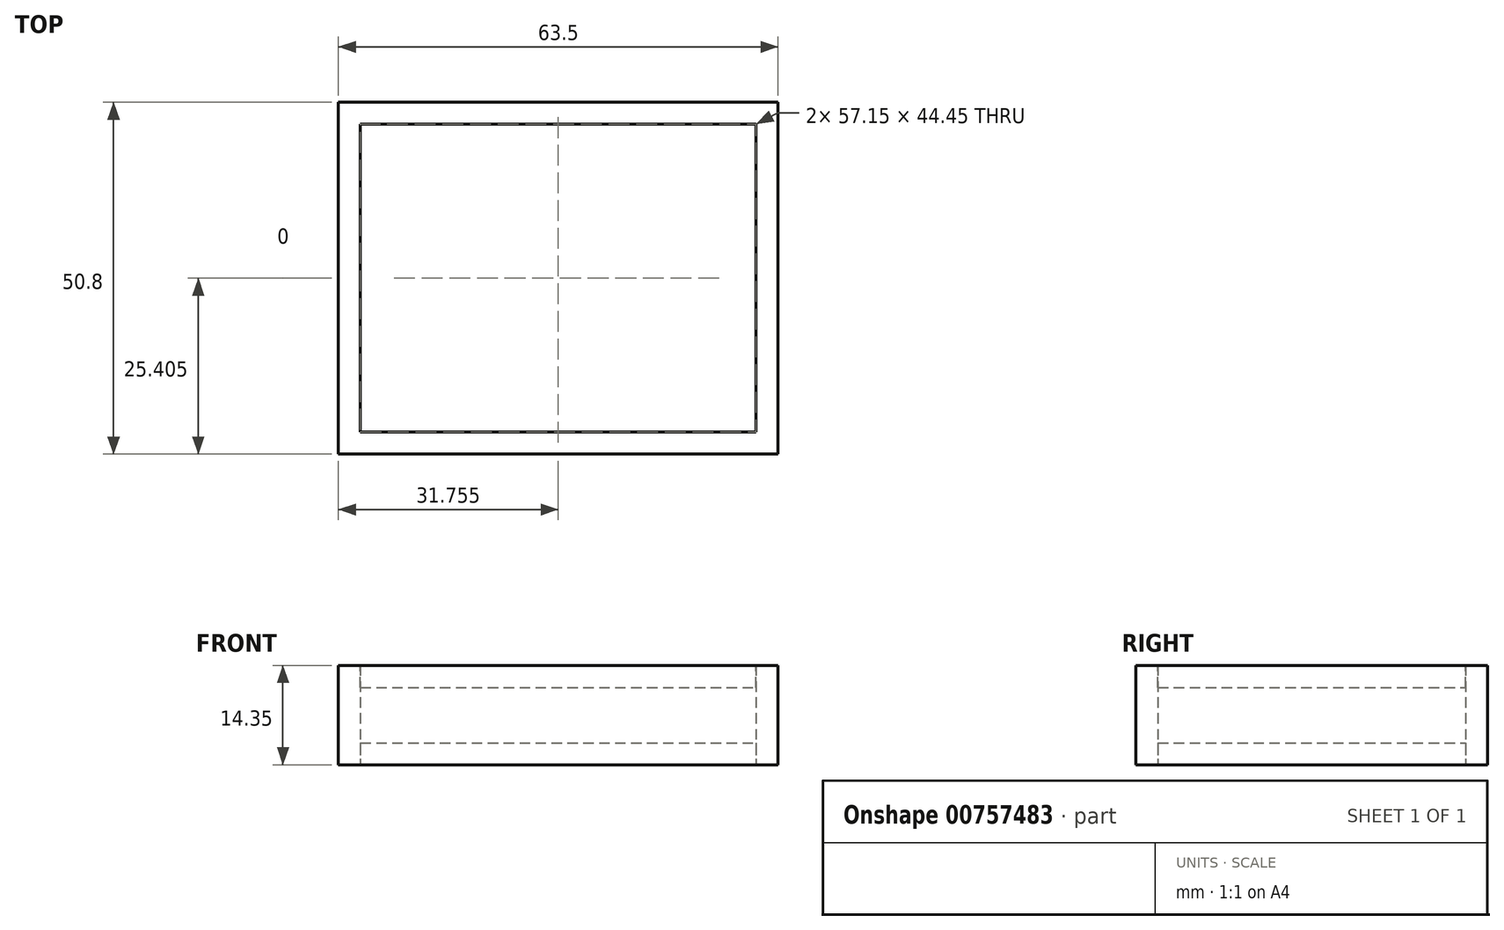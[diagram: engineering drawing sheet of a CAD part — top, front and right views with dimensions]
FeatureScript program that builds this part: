
annotation { "Feature Type Name" : "Feature", "Feature Type Description" : "" }
export const myFeature = defineFeature(function(context is Context, id is Id, definition is map)
    precondition{}
    {
        {
            var Q0;
            Q0=qCreatedBy(makeId("Top.planeOp"),FACE);
            var sketch = newSketch(context, id + "F0", { "sketchPlane" : qUnion([Q0])});
            skLineSegment(sketch, "E0.bottom", {"start": v(0, 0) * mm, "end": v(57.15, 0) * mm});
            skLineSegment(sketch, "E0.top", {"start": v(0, 44.45) * mm, "end": v(57.15, 44.45) * mm});
            skLineSegment(sketch, "E0.left", {"start": v(0, 0) * mm, "end": v(0, 44.45) * mm});
            skLineSegment(sketch, "E0.right", {"start": v(57.15, 0) * mm, "end": v(57.15, 44.45) * mm});
            skLineSegment(sketch, "E1.0", {"start": v(-3.18, 47.63) * mm, "end": v(60.32, 47.63) * mm});
            skLineSegment(sketch, "E1.1", {"start": v(-3.17, -3.17) * mm, "end": v(-3.18, 47.63) * mm});
            skLineSegment(sketch, "E1.2", {"start": v(-3.18, -3.17) * mm, "end": v(60.33, -3.17) * mm});
            skLineSegment(sketch, "E1.3", {"start": v(60.33, -3.17) * mm, "end": v(60.32, 47.62) * mm});
            skSolve(sketch);
        }
        {
            var Q0;
            Q0=makeQuery(id+"F0.imprint","IMPRINT",FACE,{"disambiguationData":[TD([[makeQuery(id+"F0.imprint","IMPRINT",EDGE,{"derivedFrom":sQuery(id+"F0.wireOp",EDGE,"E0.bottom")}),-1.0]])]});
            extrude(context, id + "F1", {"entities" : qUnion([Q0]), "depth" : 8 * mm + 6.35 * mm, "offsetDistance" : 25.4 * mm});
        }
        {
            var Q0;
            Q0=makeQuery(id+"F0.imprint","IMPRINT",FACE,{"disambiguationData":[TD([[makeQuery(id+"F0.imprint","IMPRINT",EDGE,{"derivedFrom":sQuery(id+"F0.wireOp",EDGE,"E0.bottom")}),1.0]])]});
            extrude(context, id + "F2", {"entities" : qUnion([Q0]), "depth" : 3.17 * mm, "offsetDistance" : 25.4 * mm});
        }
        {
            var Q0;
            Q0=makeQuery(id+"F1.opExtrude","CAP_FACE",FACE,{"disambiguationData":[OSD([sQuery(id+"F0.wireOp",EDGE,"E0.bottom"),sQuery(id+"F0.wireOp",EDGE,"E0.top"),sQuery(id+"F0.wireOp",EDGE,"E0.left"),sQuery(id+"F0.wireOp",EDGE,"E0.right"),sQuery(id+"F0.wireOp",EDGE,"E1.0"),sQuery(id+"F0.wireOp",EDGE,"E1.1"),sQuery(id+"F0.wireOp",EDGE,"E1.2"),sQuery(id+"F0.wireOp",EDGE,"E1.3")])],"isStart":false});
            var sketch = newSketch(context, id + "F3", { "sketchPlane" : qUnion([Q0])});
            skLineSegment(sketch, "E2.bottom", {"start": v(-3.18, 47.63) * mm, "end": v(60.33, 47.63) * mm});
            skLineSegment(sketch, "E2.top", {"start": v(-3.18, -3.17) * mm, "end": v(60.33, -3.17) * mm});
            skLineSegment(sketch, "E2.left", {"start": v(-3.18, 47.63) * mm, "end": v(-3.18, -3.17) * mm});
            skLineSegment(sketch, "E2.right", {"start": v(60.33, 47.63) * mm, "end": v(60.33, -3.17) * mm});
            skSolve(sketch);
        }
        {
            var Q0;
            Q0=makeQuery(id+"F3.imprint","IMPRINT",FACE,{"disambiguationData":[TD([[makeQuery(id+"F3.imprint","IMPRINT",EDGE,{"derivedFrom":makeQuery(id+"F1.opExtrude","CAP_EDGE",EDGE,{"disambiguationData":[OSD([sQuery(id+"F0.wireOp",EDGE,"E0.bottom")])],"isStart":false})}),1.0]])]});
            extrude(context, id + "F4", {"entities" : qUnion([Q0]), "oppositeDirection" : true, "depth" : 3.17 * mm, "offsetDistance" : 25.4 * mm});
        }
    });
